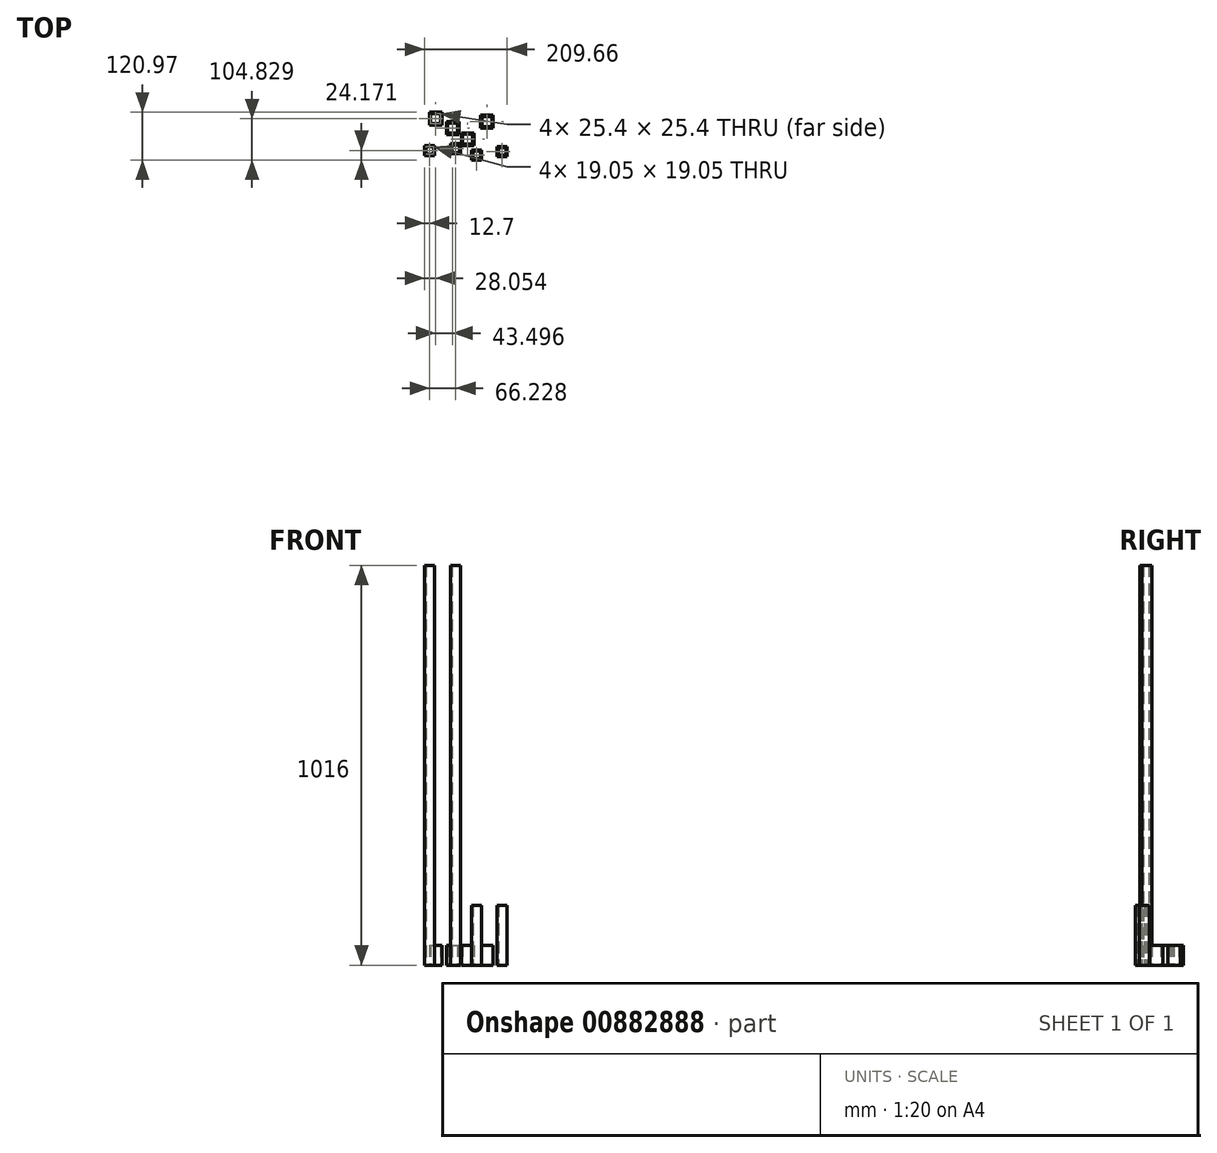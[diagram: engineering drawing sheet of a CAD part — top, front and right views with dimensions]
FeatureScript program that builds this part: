
annotation { "Feature Type Name" : "Feature", "Feature Type Description" : "" }
export const myFeature = defineFeature(function(context is Context, id is Id, definition is map)
    precondition{}
    {
        {
            var Q0;
            Q0=qCreatedBy(makeId("Top.planeOp"),FACE);
            var sketch = newSketch(context, id + "F0", { "sketchPlane" : qUnion([Q0])});
            skLineSegment(sketch, "E0.bottom", {"start": v(-117.16, 28.52) * mm, "end": v(-91.76, 28.52) * mm});
            skLineSegment(sketch, "E0.top", {"start": v(-117.16, 3.12) * mm, "end": v(-91.76, 3.12) * mm});
            skLineSegment(sketch, "E0.left", {"start": v(-117.16, 28.52) * mm, "end": v(-117.16, 3.12) * mm});
            skLineSegment(sketch, "E0.right", {"start": v(-91.76, 28.52) * mm, "end": v(-91.76, 3.12) * mm});
            skPoint(sketch, "E0.middle", {"position": v(-104.46, 15.82) * mm});
            skLineSegment(sketch, "E1.bottom", {"start": v(-120.33, 31.97) * mm, "end": v(-88.58, 31.97) * mm});
            skLineSegment(sketch, "E1.top", {"start": v(-120.33, -0.32) * mm, "end": v(-88.58, -0.32) * mm});
            skLineSegment(sketch, "E1.left", {"start": v(-120.33, 31.97) * mm, "end": v(-120.33, -0.32) * mm});
            skLineSegment(sketch, "E1.right", {"start": v(-88.58, 31.97) * mm, "end": v(-88.58, -0.32) * mm});
            skSolve(sketch);
        }
        {
            var Q0;
            Q0=qCreatedBy(makeId("Top.planeOp"),FACE);
            var sketch = newSketch(context, id + "F1", { "sketchPlane" : qUnion([Q0])});
            skLineSegment(sketch, "E2.bottom", {"start": v(-160.66, 52.66) * mm, "end": v(-135.26, 52.66) * mm});
            skLineSegment(sketch, "E2.top", {"start": v(-160.66, 27.26) * mm, "end": v(-135.26, 27.26) * mm});
            skLineSegment(sketch, "E2.left", {"start": v(-160.66, 52.66) * mm, "end": v(-160.66, 27.26) * mm});
            skLineSegment(sketch, "E2.right", {"start": v(-135.26, 52.66) * mm, "end": v(-135.26, 27.26) * mm});
            skPoint(sketch, "E2.middle", {"position": v(-147.96, 39.96) * mm});
            skLineSegment(sketch, "E3.bottom", {"start": v(-163.83, 56.1) * mm, "end": v(-132.08, 56.1) * mm});
            skLineSegment(sketch, "E3.top", {"start": v(-163.83, 23.81) * mm, "end": v(-132.08, 23.81) * mm});
            skLineSegment(sketch, "E3.left", {"start": v(-163.83, 56.1) * mm, "end": v(-163.83, 23.81) * mm});
            skLineSegment(sketch, "E3.right", {"start": v(-132.08, 56.1) * mm, "end": v(-132.08, 23.81) * mm});
            skSolve(sketch);
        }
        {
            var Q0;
            Q0=qCreatedBy(makeId("Top.planeOp"),FACE);
            var sketch = newSketch(context, id + "F2", { "sketchPlane" : qUnion([Q0])});
            skLineSegment(sketch, "E4.bottom", {"start": v(-30.6, 45.26) * mm, "end": v(-5.2, 45.26) * mm});
            skLineSegment(sketch, "E4.top", {"start": v(-30.6, 19.86) * mm, "end": v(-5.2, 19.86) * mm});
            skLineSegment(sketch, "E4.left", {"start": v(-30.6, 45.26) * mm, "end": v(-30.6, 19.86) * mm});
            skLineSegment(sketch, "E4.right", {"start": v(-5.2, 45.26) * mm, "end": v(-5.2, 19.86) * mm});
            skPoint(sketch, "E4.middle", {"position": v(-17.9, 32.56) * mm});
            skLineSegment(sketch, "E5.bottom", {"start": v(-33.78, 48.7) * mm, "end": v(-2.03, 48.7) * mm});
            skLineSegment(sketch, "E5.top", {"start": v(-33.78, 16.41) * mm, "end": v(-2.03, 16.41) * mm});
            skLineSegment(sketch, "E5.left", {"start": v(-33.78, 48.7) * mm, "end": v(-33.78, 16.41) * mm});
            skLineSegment(sketch, "E5.right", {"start": v(-2.03, 48.7) * mm, "end": v(-2.03, 16.41) * mm});
            skSolve(sketch);
        }
        {
            var Q0;
            Q0=qCreatedBy(makeId("Top.planeOp"),FACE);
            var sketch = newSketch(context, id + "F3", { "sketchPlane" : qUnion([Q0])});
            skLineSegment(sketch, "E6.bottom", {"start": v(-79.26, 0.5) * mm, "end": v(-53.86, 0.5) * mm});
            skLineSegment(sketch, "E6.top", {"start": v(-79.26, -24.9) * mm, "end": v(-53.86, -24.9) * mm});
            skLineSegment(sketch, "E6.left", {"start": v(-79.26, 0.5) * mm, "end": v(-79.26, -24.9) * mm});
            skLineSegment(sketch, "E6.right", {"start": v(-53.86, 0.5) * mm, "end": v(-53.86, -24.9) * mm});
            skPoint(sketch, "E6.middle", {"position": v(-66.56, -12.2) * mm});
            skLineSegment(sketch, "E7.bottom", {"start": v(-82.43, 3.94) * mm, "end": v(-50.68, 3.94) * mm});
            skLineSegment(sketch, "E7.top", {"start": v(-82.43, -28.36) * mm, "end": v(-50.68, -28.36) * mm});
            skLineSegment(sketch, "E7.left", {"start": v(-82.43, 3.94) * mm, "end": v(-82.43, -28.36) * mm});
            skLineSegment(sketch, "E7.right", {"start": v(-50.68, 3.94) * mm, "end": v(-50.68, -28.36) * mm});
            skSolve(sketch);
        }
        {
            var Q0;
            Q0=makeQuery(id+"F1.imprint","IMPRINT",FACE,{"disambiguationData":[TD([[makeQuery(id+"F1.imprint","IMPRINT",EDGE,{"derivedFrom":sQuery(id+"F1.wireOp",EDGE,"E2.bottom")}),1.0]])]});
            var Q1;
            Q1=makeQuery(id+"F0.imprint","IMPRINT",FACE,{"disambiguationData":[TD([[makeQuery(id+"F0.imprint","IMPRINT",EDGE,{"derivedFrom":sQuery(id+"F0.wireOp",EDGE,"E0.bottom")}),1.0]])]});
            var Q2;
            Q2=makeQuery(id+"F3.imprint","IMPRINT",FACE,{"disambiguationData":[TD([[makeQuery(id+"F3.imprint","IMPRINT",EDGE,{"derivedFrom":sQuery(id+"F3.wireOp",EDGE,"E6.bottom")}),1.0]])]});
            var Q3;
            Q3=makeQuery(id+"F2.imprint","IMPRINT",FACE,{"disambiguationData":[TD([[makeQuery(id+"F2.imprint","IMPRINT",EDGE,{"derivedFrom":sQuery(id+"F2.wireOp",EDGE,"E4.bottom")}),1.0]])]});
            extrude(context, id + "F4", {"entities" : qUnion([Q0, Q1, Q2, Q3]), "depth" : 50.8 * mm, "offsetDistance" : 25.4 * mm});
        }
        {
            var Q0;
            Q0=qCreatedBy(makeId("Top.planeOp"),FACE);
            var sketch = newSketch(context, id + "F5", { "sketchPlane" : qUnion([Q0])});
            skLineSegment(sketch, "E8.bottom", {"start": v(-150.61, -28) * mm, "end": v(-176.01, -28) * mm});
            skLineSegment(sketch, "E8.top", {"start": v(-150.61, -53.4) * mm, "end": v(-176.01, -53.4) * mm});
            skLineSegment(sketch, "E8.left", {"start": v(-150.61, -28) * mm, "end": v(-150.61, -53.4) * mm});
            skLineSegment(sketch, "E8.right", {"start": v(-176.01, -28) * mm, "end": v(-176.01, -53.4) * mm});
            skPoint(sketch, "E8.middle", {"position": v(-163.31, -40.7) * mm});
            skLineSegment(sketch, "E9.bottom", {"start": v(-153.79, -31.17) * mm, "end": v(-172.84, -31.17) * mm});
            skLineSegment(sketch, "E9.top", {"start": v(-153.79, -50.22) * mm, "end": v(-172.84, -50.22) * mm});
            skLineSegment(sketch, "E9.left", {"start": v(-153.79, -31.17) * mm, "end": v(-153.79, -50.22) * mm});
            skLineSegment(sketch, "E9.right", {"start": v(-172.84, -31.17) * mm, "end": v(-172.84, -50.22) * mm});
            skSolve(sketch);
        }
        {
            var Q0;
            Q0=qCreatedBy(makeId("Top.planeOp"),FACE);
            var sketch = newSketch(context, id + "F6", { "sketchPlane" : qUnion([Q0])});
            skLineSegment(sketch, "E10.bottom", {"start": v(-84.38, -23.37) * mm, "end": v(-109.78, -23.37) * mm});
            skLineSegment(sketch, "E10.top", {"start": v(-84.38, -48.77) * mm, "end": v(-109.78, -48.77) * mm});
            skLineSegment(sketch, "E10.left", {"start": v(-84.38, -23.37) * mm, "end": v(-84.38, -48.77) * mm});
            skLineSegment(sketch, "E10.right", {"start": v(-109.78, -23.37) * mm, "end": v(-109.78, -48.77) * mm});
            skPoint(sketch, "E10.middle", {"position": v(-97.08, -36.07) * mm});
            skLineSegment(sketch, "E11.bottom", {"start": v(-87.56, -26.55) * mm, "end": v(-106.6, -26.55) * mm});
            skLineSegment(sketch, "E11.top", {"start": v(-87.56, -45.6) * mm, "end": v(-106.6, -45.6) * mm});
            skLineSegment(sketch, "E11.left", {"start": v(-87.56, -26.55) * mm, "end": v(-87.56, -45.6) * mm});
            skLineSegment(sketch, "E11.right", {"start": v(-106.6, -26.55) * mm, "end": v(-106.6, -45.6) * mm});
            skSolve(sketch);
        }
        {
            var Q0;
            Q0=qCreatedBy(makeId("Top.planeOp"),FACE);
            var sketch = newSketch(context, id + "F7", { "sketchPlane" : qUnion([Q0])});
            skLineSegment(sketch, "E12.bottom", {"start": v(-31.19, -39.47) * mm, "end": v(-56.59, -39.47) * mm});
            skLineSegment(sketch, "E12.top", {"start": v(-31.19, -64.87) * mm, "end": v(-56.59, -64.87) * mm});
            skLineSegment(sketch, "E12.left", {"start": v(-31.19, -39.47) * mm, "end": v(-31.19, -64.87) * mm});
            skLineSegment(sketch, "E12.right", {"start": v(-56.59, -39.47) * mm, "end": v(-56.59, -64.87) * mm});
            skPoint(sketch, "E12.middle", {"position": v(-43.89, -52.17) * mm});
            skLineSegment(sketch, "E13.bottom", {"start": v(-34.36, -42.64) * mm, "end": v(-53.41, -42.64) * mm});
            skLineSegment(sketch, "E13.top", {"start": v(-34.36, -61.7) * mm, "end": v(-53.41, -61.7) * mm});
            skLineSegment(sketch, "E13.left", {"start": v(-34.36, -42.64) * mm, "end": v(-34.36, -61.7) * mm});
            skLineSegment(sketch, "E13.right", {"start": v(-53.41, -42.64) * mm, "end": v(-53.41, -61.7) * mm});
            skSolve(sketch);
        }
        {
            var Q0;
            Q0=qCreatedBy(makeId("Top.planeOp"),FACE);
            var sketch = newSketch(context, id + "F8", { "sketchPlane" : qUnion([Q0])});
            skLineSegment(sketch, "E14.bottom", {"start": v(33.65, -30.4) * mm, "end": v(8.25, -30.4) * mm});
            skLineSegment(sketch, "E14.top", {"start": v(33.65, -55.8) * mm, "end": v(8.25, -55.8) * mm});
            skLineSegment(sketch, "E14.left", {"start": v(33.65, -30.4) * mm, "end": v(33.65, -55.8) * mm});
            skLineSegment(sketch, "E14.right", {"start": v(8.25, -30.4) * mm, "end": v(8.25, -55.8) * mm});
            skPoint(sketch, "E14.middle", {"position": v(20.95, -43.1) * mm});
            skLineSegment(sketch, "E15.bottom", {"start": v(30.48, -33.58) * mm, "end": v(11.43, -33.58) * mm});
            skLineSegment(sketch, "E15.top", {"start": v(30.48, -52.63) * mm, "end": v(11.43, -52.63) * mm});
            skLineSegment(sketch, "E15.left", {"start": v(30.48, -33.58) * mm, "end": v(30.48, -52.63) * mm});
            skLineSegment(sketch, "E15.right", {"start": v(11.43, -33.58) * mm, "end": v(11.43, -52.63) * mm});
            skSolve(sketch);
        }
        {
            var Q0;
            Q0=makeQuery(id+"F8.imprint","IMPRINT",FACE,{"disambiguationData":[TD([[makeQuery(id+"F8.imprint","IMPRINT",EDGE,{"derivedFrom":sQuery(id+"F8.wireOp",EDGE,"E14.bottom")}),1.0]])]});
            var Q1;
            Q1=makeQuery(id+"F7.imprint","IMPRINT",FACE,{"disambiguationData":[TD([[makeQuery(id+"F7.imprint","IMPRINT",EDGE,{"derivedFrom":sQuery(id+"F7.wireOp",EDGE,"E12.bottom")}),1.0]])]});
            extrude(context, id + "F9", {"entities" : qUnion([Q0, Q1]), "depth" : 152.4 * mm, "offsetDistance" : 25.4 * mm});
        }
        {
            var Q0;
            Q0=makeQuery(id+"F6.imprint","IMPRINT",FACE,{"disambiguationData":[TD([[makeQuery(id+"F6.imprint","IMPRINT",EDGE,{"derivedFrom":sQuery(id+"F6.wireOp",EDGE,"E10.bottom")}),1.0]])]});
            var Q1;
            Q1=makeQuery(id+"F5.imprint","IMPRINT",FACE,{"disambiguationData":[TD([[makeQuery(id+"F5.imprint","IMPRINT",EDGE,{"derivedFrom":sQuery(id+"F5.wireOp",EDGE,"E8.bottom")}),1.0]])]});
            extrude(context, id + "F10", {"entities" : qUnion([Q0, Q1]), "depth" : 1016 * mm, "offsetDistance" : 25.4 * mm});
        }
    });
